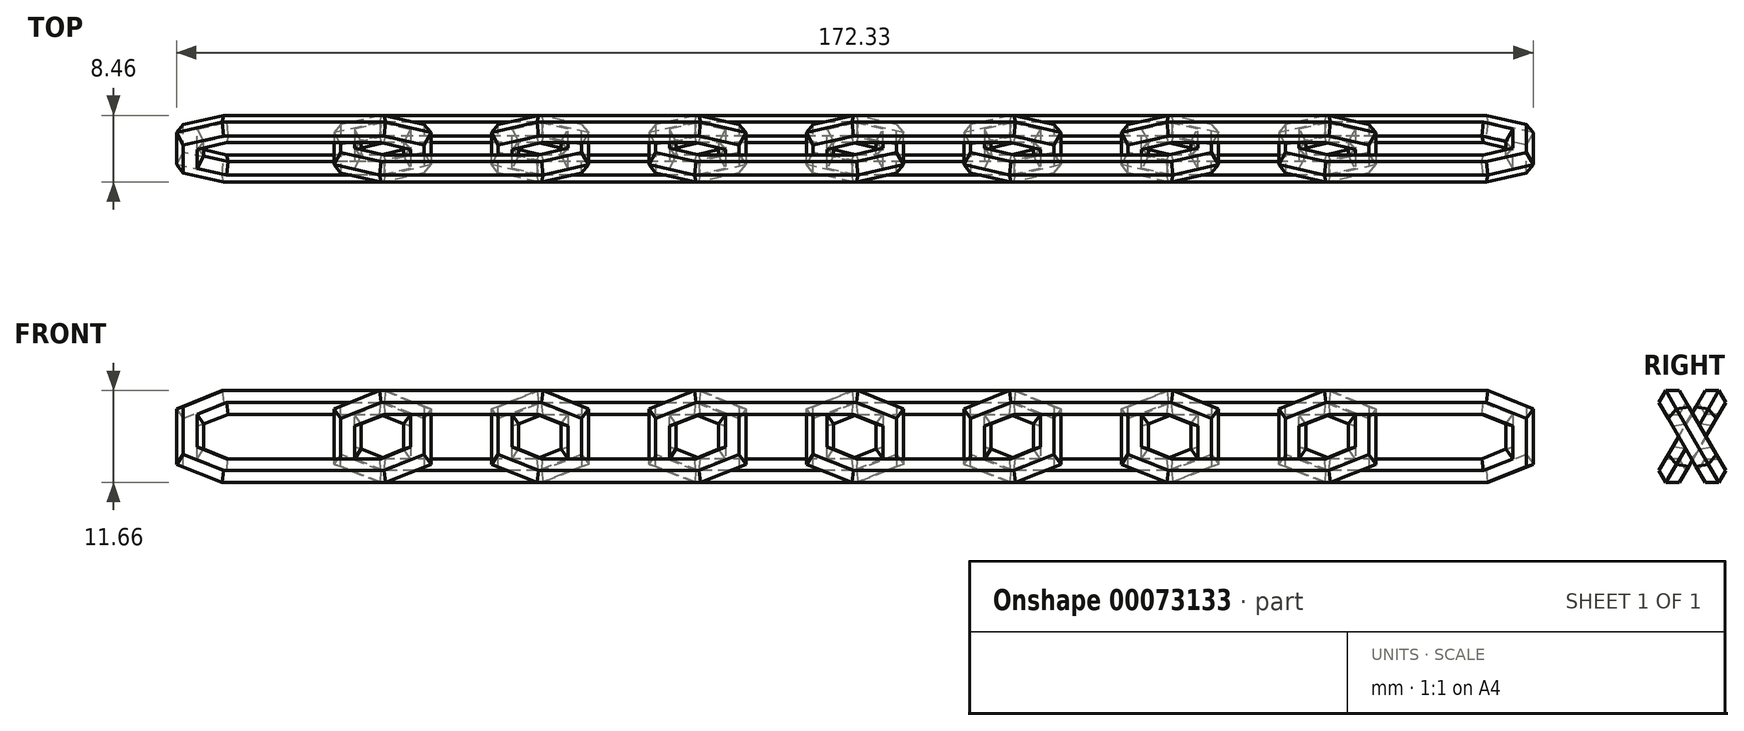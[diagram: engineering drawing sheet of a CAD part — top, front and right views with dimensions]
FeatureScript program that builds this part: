
annotation { "Feature Type Name" : "Feature", "Feature Type Description" : "" }
export const myFeature = defineFeature(function(context is Context, id is Id, definition is map)
    precondition{}
    {
        {
            var Q0;
            Q0=qCreatedBy(makeId("Front.planeOp"),FACE);
            var sketch = newSketch(context, id + "F0", { "sketchPlane" : qUnion([Q0])});
            skCircle(sketch, "E0.cCircle", {"center": v(-58.85, 0) * mm, "radius": 1.5 * mm, "construction": true});
            skLineSegment(sketch, "E0.0", {"start": v(-57.98, 1.5) * mm, "end": v(-57.12, 0) * mm});
            skLineSegment(sketch, "E0.1", {"start": v(-57.12, 0) * mm, "end": v(-57.98, -1.5) * mm});
            skLineSegment(sketch, "E0.2", {"start": v(-57.98, -1.5) * mm, "end": v(-59.72, -1.5) * mm});
            skLineSegment(sketch, "E0.3", {"start": v(-59.72, -1.5) * mm, "end": v(-60.58, 0) * mm});
            skLineSegment(sketch, "E0.4", {"start": v(-60.58, 0) * mm, "end": v(-59.72, 1.5) * mm});
            skLineSegment(sketch, "E0.5", {"start": v(-59.72, 1.5) * mm, "end": v(-57.98, 1.5) * mm});
            skPoint(sketch, "E0.0.midPoint", {"position": v(-57.55, 0.75) * mm});
            skSolve(sketch);
        }
        {
            var Q0;
            Q0=qCreatedBy(makeId("Top.planeOp"),FACE);
            var sketch = newSketch(context, id + "F1", { "sketchPlane" : qUnion([Q0])});
            skLineSegment(sketch, "E1.rect.bottom", {"start": v(-83.28, 5) * mm, "end": v(-63.28, 5) * mm});
            skLineSegment(sketch, "E1.rect.top", {"start": v(-83.28, -5) * mm, "end": v(-63.28, -5) * mm});
            skLineSegment(sketch, "E1.rect.left", {"start": v(-83.28, 5) * mm, "end": v(-83.28, -5) * mm, "construction": true});
            skLineSegment(sketch, "E1.rect.right", {"start": v(-63.28, 5) * mm, "end": v(-63.28, -5) * mm, "construction": true});
            skPoint(sketch, "E1.rect.middle", {"position": v(-73.28, 0) * mm});
            skLineSegment(sketch, "E2", {"start": v(-73.28, 0) * mm, "end": v(-58.85, 0) * mm, "construction": true});
            skPoint(sketch, "E2.endSnap0", {"position": v(-58.85, 0) * mm});
            skLineSegment(sketch, "E3", {"start": v(-63.28, -5) * mm, "end": v(-58.85, -2.95) * mm});
            skLineSegment(sketch, "E4", {"start": v(-58.85, -2.95) * mm, "end": v(-58.85, 2.95) * mm});
            skLineSegment(sketch, "E5", {"start": v(-58.85, 2.95) * mm, "end": v(-63.28, 5) * mm});
            skLineSegment(sketch, "E6", {"start": v(-73.28, -5) * mm, "end": v(-73.28, 5) * mm, "construction": true});
            skLineSegment(sketch, "E7.MirrorCS", {"start": v(-87.71, 2.95) * mm, "end": v(-83.28, 5) * mm});
            skLineSegment(sketch, "E8.MirrorCS", {"start": v(-87.71, -2.95) * mm, "end": v(-87.71, 2.95) * mm});
            skLineSegment(sketch, "E9.MirrorCS", {"start": v(-83.28, -5) * mm, "end": v(-87.71, -2.95) * mm});
            skSolve(sketch);
        }
        {
            var Q0;
            Q0=makeQuery(id+"F0.imprint","IMPRINT",FACE,{"disambiguationData":[TD([[makeQuery(id+"F0.imprint","IMPRINT",EDGE,{"derivedFrom":sQuery(id+"F0.wireOp",EDGE,"E0.0")}),-1.0]])]});
            var Q1;
            Q1 = qConstructionFilter(qBodyType(qCreatedBy(id + "F1" ,EDGE), BodyType.WIRE), ConstructionObject.NO);
            sweep(context, id + "F2", {"profiles" : qUnion([Q0]), "path" : qUnion([Q1])});
        }
        {
            var Q0;
            Q0=makeQuery(id+"F2.opSweep","SWEPT_BODY",BODY,{"disambiguationData":[OSD([sQuery(id+"F0.wireOp",EDGE,"E0.0"),sQuery(id+"F0.wireOp",EDGE,"E0.1"),sQuery(id+"F0.wireOp",EDGE,"E0.2"),sQuery(id+"F0.wireOp",EDGE,"E0.3"),sQuery(id+"F0.wireOp",EDGE,"E0.4"),sQuery(id+"F0.wireOp",EDGE,"E0.5"),sQuery(id+"F1.wireOp",EDGE,"E9.MirrorCS")])]});
            var Q1;
            Q1=sQuery(id+"F1.wireOp",EDGE,"E2");
            transform(context, id + "F3", {"entities" : qUnion([Q0]), "transformType" : TransformType.ROTATION, "transformAxis" : qUnion([Q1]), "angle" : 60 * degree, "makeCopy" : false});
        }
        {
            var Q0;
            Q0=makeQuery(id+"F2.opSweep","SWEPT_BODY",BODY,{"disambiguationData":[OSD([sQuery(id+"F0.wireOp",EDGE,"E0.0"),sQuery(id+"F0.wireOp",EDGE,"E0.1"),sQuery(id+"F0.wireOp",EDGE,"E0.2"),sQuery(id+"F0.wireOp",EDGE,"E0.3"),sQuery(id+"F0.wireOp",EDGE,"E0.4"),sQuery(id+"F0.wireOp",EDGE,"E0.5"),sQuery(id+"F1.wireOp",EDGE,"E9.MirrorCS")])]});
            var Q1;
            Q1=qCreatedBy(makeId("Front.planeOp"),FACE);
            mirror(context, id + "F4", {"entities" : qUnion([Q0]), "mirrorPlane" : qUnion([Q1])});
        }
        {
            var Q0;
            Q0=makeQuery(id+"F4.opPattern","COPY",BODY,{"derivedFrom":makeQuery(id+"F2.opSweep","SWEPT_BODY",BODY,{"disambiguationData":[OSD([sQuery(id+"F0.wireOp",EDGE,"E0.0"),sQuery(id+"F0.wireOp",EDGE,"E0.1"),sQuery(id+"F0.wireOp",EDGE,"E0.2"),sQuery(id+"F0.wireOp",EDGE,"E0.3"),sQuery(id+"F0.wireOp",EDGE,"E0.4"),sQuery(id+"F0.wireOp",EDGE,"E0.5"),sQuery(id+"F1.wireOp",EDGE,"E9.MirrorCS")])]}),"instanceName":"1"});
            transform(context, id + "F5", {"entities" : qUnion([Q0]), "transformType" : TransformType.TRANSLATION_3D, "dx" : 20 * mm, "dy" : 0 * mm, "dz" : 0 * mm, "makeCopy" : false});
        }
        {
            var Q0;
            Q0=makeQuery(id+"F2.opSweep","SWEPT_BODY",BODY,{"disambiguationData":[OSD([sQuery(id+"F0.wireOp",EDGE,"E0.0"),sQuery(id+"F0.wireOp",EDGE,"E0.1"),sQuery(id+"F0.wireOp",EDGE,"E0.2"),sQuery(id+"F0.wireOp",EDGE,"E0.3"),sQuery(id+"F0.wireOp",EDGE,"E0.4"),sQuery(id+"F0.wireOp",EDGE,"E0.5"),sQuery(id+"F1.wireOp",EDGE,"E9.MirrorCS")])]});
            var Q1;
            Q1=makeQuery(id+"F4.opPattern","COPY",BODY,{"derivedFrom":makeQuery(id+"F2.opSweep","SWEPT_BODY",BODY,{"disambiguationData":[OSD([sQuery(id+"F0.wireOp",EDGE,"E0.0"),sQuery(id+"F0.wireOp",EDGE,"E0.1"),sQuery(id+"F0.wireOp",EDGE,"E0.2"),sQuery(id+"F0.wireOp",EDGE,"E0.3"),sQuery(id+"F0.wireOp",EDGE,"E0.4"),sQuery(id+"F0.wireOp",EDGE,"E0.5"),sQuery(id+"F1.wireOp",EDGE,"E9.MirrorCS")])]}),"instanceName":"1"});
            transform(context, id + "F6", {"entities" : qUnion([Q0, Q1]), "transformType" : TransformType.TRANSLATION_3D, "dx" : 40 * mm, "dy" : 0 * mm, "dz" : 0 * mm, "makeCopy" : true});
        }
        {
            var Q0;
            Q0=makeQuery(id+"F2.opSweep","SWEPT_BODY",BODY,{"disambiguationData":[OSD([sQuery(id+"F0.wireOp",EDGE,"E0.0"),sQuery(id+"F0.wireOp",EDGE,"E0.1"),sQuery(id+"F0.wireOp",EDGE,"E0.2"),sQuery(id+"F0.wireOp",EDGE,"E0.3"),sQuery(id+"F0.wireOp",EDGE,"E0.4"),sQuery(id+"F0.wireOp",EDGE,"E0.5"),sQuery(id+"F1.wireOp",EDGE,"E9.MirrorCS")])]});
            var Q1;
            Q1=makeQuery(id+"F4.opPattern","COPY",BODY,{"derivedFrom":makeQuery(id+"F2.opSweep","SWEPT_BODY",BODY,{"disambiguationData":[OSD([sQuery(id+"F0.wireOp",EDGE,"E0.0"),sQuery(id+"F0.wireOp",EDGE,"E0.1"),sQuery(id+"F0.wireOp",EDGE,"E0.2"),sQuery(id+"F0.wireOp",EDGE,"E0.3"),sQuery(id+"F0.wireOp",EDGE,"E0.4"),sQuery(id+"F0.wireOp",EDGE,"E0.5"),sQuery(id+"F1.wireOp",EDGE,"E9.MirrorCS")])]}),"instanceName":"1"});
            var Q2;
            Q2=makeQuery(id+"F6.opPattern","COPY",BODY,{"derivedFrom":makeQuery(id+"F2.opSweep","SWEPT_BODY",BODY,{"disambiguationData":[OSD([sQuery(id+"F0.wireOp",EDGE,"E0.0"),sQuery(id+"F0.wireOp",EDGE,"E0.1"),sQuery(id+"F0.wireOp",EDGE,"E0.2"),sQuery(id+"F0.wireOp",EDGE,"E0.3"),sQuery(id+"F0.wireOp",EDGE,"E0.4"),sQuery(id+"F0.wireOp",EDGE,"E0.5"),sQuery(id+"F1.wireOp",EDGE,"E9.MirrorCS")])]}),"instanceName":"1"});
            var Q3;
            Q3=makeQuery(id+"F6.opPattern","COPY",BODY,{"derivedFrom":makeQuery(id+"F4.opPattern","COPY",BODY,{"derivedFrom":makeQuery(id+"F2.opSweep","SWEPT_BODY",BODY,{"disambiguationData":[OSD([sQuery(id+"F0.wireOp",EDGE,"E0.0"),sQuery(id+"F0.wireOp",EDGE,"E0.1"),sQuery(id+"F0.wireOp",EDGE,"E0.2"),sQuery(id+"F0.wireOp",EDGE,"E0.3"),sQuery(id+"F0.wireOp",EDGE,"E0.4"),sQuery(id+"F0.wireOp",EDGE,"E0.5"),sQuery(id+"F1.wireOp",EDGE,"E9.MirrorCS")])]}),"instanceName":"1"}),"instanceName":"1"});
            transform(context, id + "F7", {"entities" : qUnion([Q0, Q1, Q2, Q3]), "transformType" : TransformType.TRANSLATION_3D, "dx" : 80 * mm, "dy" : 0 * mm, "dz" : 0 * mm, "makeCopy" : true});
        }
    });
